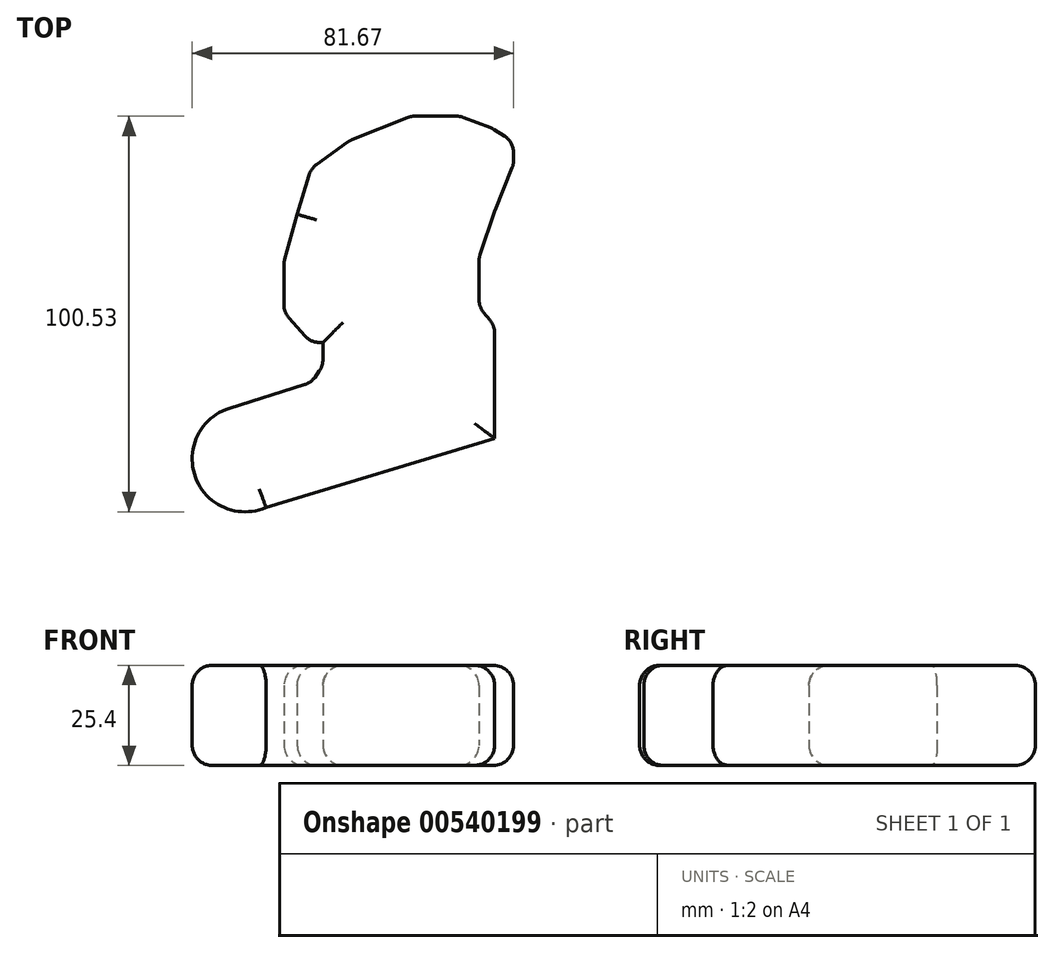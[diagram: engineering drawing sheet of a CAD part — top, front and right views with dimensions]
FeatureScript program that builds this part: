
annotation { "Feature Type Name" : "Feature", "Feature Type Description" : "" }
export const myFeature = defineFeature(function(context is Context, id is Id, definition is map)
    precondition{}
    {
        {
            var Q0;
            Q0=qCreatedBy(makeId("Top.planeOp"),FACE);
            var sketch = newSketch(context, id + "F0", { "sketchPlane" : qUnion([Q0])});
            skLineSegment(sketch, "E0", {"start": v(-11.4, -55.6) * mm, "end": v(46.68, -38.04) * mm});
            skLineSegment(sketch, "E1", {"start": v(46.68, -38.04) * mm, "end": v(46.68, -9.43) * mm});
            skLineSegment(sketch, "E2", {"start": v(46.68, -9.43) * mm, "end": v(42.72, -4.61) * mm});
            skLineSegment(sketch, "E3", {"start": v(42.72, -4.61) * mm, "end": v(42.72, 7.85) * mm});
            skLineSegment(sketch, "E4", {"start": v(42.72, 7.85) * mm, "end": v(46.68, 19.75) * mm});
            skLineSegment(sketch, "E5", {"start": v(46.68, 19.75) * mm, "end": v(51.5, 31.65) * mm});
            skLineSegment(sketch, "E6", {"start": v(51.5, 31.65) * mm, "end": v(51.5, 37.31) * mm});
            skLineSegment(sketch, "E7", {"start": v(0, -23.88) * mm, "end": v(-20.74, -30.4) * mm});
            skArc(sketch, "E8", {"start": v(-20.74, -30.4) * mm, "mid": v(-29.33, -47.91) * mm, "end": v(-11.4, -55.6) * mm});
            skLineSegment(sketch, "E9", {"start": v(0, -23.88) * mm, "end": v(3.06, -19.63) * mm});
            skLineSegment(sketch, "E10", {"start": v(3.06, -19.63) * mm, "end": v(3.06, -13.68) * mm});
            skLineSegment(sketch, "E11", {"start": v(3.06, -13.68) * mm, "end": v(0, -13.68) * mm});
            skLineSegment(sketch, "E12", {"start": v(0, -13.68) * mm, "end": v(-6.86, -6.03) * mm});
            skLineSegment(sketch, "E13", {"start": v(-6.86, -6.03) * mm, "end": v(-6.86, 6.72) * mm});
            skLineSegment(sketch, "E14", {"start": v(-6.86, 6.72) * mm, "end": v(-3.46, 18.9) * mm});
            skLineSegment(sketch, "E15", {"start": v(-3.46, 18.9) * mm, "end": v(0, 30.51) * mm});
            skLineSegment(sketch, "E16", {"start": v(0, 30.51) * mm, "end": v(9.85, 37.6) * mm});
            skLineSegment(sketch, "E17", {"start": v(9.85, 37.6) * mm, "end": v(25.44, 43.83) * mm});
            skLineSegment(sketch, "E18", {"start": v(25.44, 43.83) * mm, "end": v(37.9, 43.83) * mm});
            skLineSegment(sketch, "E19", {"start": v(37.9, 43.83) * mm, "end": v(46.11, 40.71) * mm});
            skLineSegment(sketch, "E20", {"start": v(46.11, 40.71) * mm, "end": v(51.5, 37.31) * mm});
            skSolve(sketch);
        }
        {
            var Q0;
            Q0=makeQuery(id+"F0.imprint","IMPRINT",FACE,{"disambiguationData":[TD([[makeQuery(id+"F0.imprint","IMPRINT",EDGE,{"derivedFrom":sQuery(id+"F0.wireOp",EDGE,"E0")}),1.0]])]});
            extrude(context, id + "F1", {"entities" : qUnion([Q0]), "depth" : 25.4 * mm, "offsetDistance" : 25.4 * mm});
        }
        {
            var Q0;
            Q0=makeQuery(id+"F1.opExtrude","SWEPT_EDGE",EDGE,{"disambiguationData":[OSD([sQuery(id+"F0.wireOp",EDGE,"E16"),sQuery(id+"F0.wireOp",EDGE,"E17")])]});
            var Q1;
            Q1=makeQuery(id+"F1.opExtrude","SWEPT_EDGE",EDGE,{"disambiguationData":[OSD([sQuery(id+"F0.wireOp",EDGE,"E17"),sQuery(id+"F0.wireOp",EDGE,"E18")])]});
            var Q2;
            Q2=makeQuery(id+"F1.opExtrude","SWEPT_EDGE",EDGE,{"disambiguationData":[OSD([sQuery(id+"F0.wireOp",EDGE,"E15"),sQuery(id+"F0.wireOp",EDGE,"E16")])]});
            var Q3;
            Q3=makeQuery(id+"F1.opExtrude","SWEPT_EDGE",EDGE,{"disambiguationData":[OSD([sQuery(id+"F0.wireOp",EDGE,"E13"),sQuery(id+"F0.wireOp",EDGE,"E14")])]});
            var Q4;
            Q4=makeQuery(id+"F1.opExtrude","SWEPT_EDGE",EDGE,{"disambiguationData":[OSD([sQuery(id+"F0.wireOp",EDGE,"E12"),sQuery(id+"F0.wireOp",EDGE,"E13")])]});
            var Q5;
            Q5=makeQuery(id+"F1.opExtrude","SWEPT_EDGE",EDGE,{"disambiguationData":[OSD([sQuery(id+"F0.wireOp",EDGE,"E11"),sQuery(id+"F0.wireOp",EDGE,"E12")])]});
            var Q6;
            Q6=makeQuery(id+"F1.opExtrude","SWEPT_EDGE",EDGE,{"disambiguationData":[OSD([sQuery(id+"F0.wireOp",EDGE,"E7"),sQuery(id+"F0.wireOp",EDGE,"E9")])]});
            var Q7;
            Q7=makeQuery(id+"F1.opExtrude","SWEPT_EDGE",EDGE,{"disambiguationData":[OSD([sQuery(id+"F0.wireOp",EDGE,"E2"),sQuery(id+"F0.wireOp",EDGE,"E3")])]});
            var Q8;
            Q8=makeQuery(id+"F1.opExtrude","SWEPT_EDGE",EDGE,{"disambiguationData":[OSD([sQuery(id+"F0.wireOp",EDGE,"E3"),sQuery(id+"F0.wireOp",EDGE,"E4")])]});
            var Q9;
            Q9=makeQuery(id+"F1.opExtrude","SWEPT_EDGE",EDGE,{"disambiguationData":[OSD([sQuery(id+"F0.wireOp",EDGE,"E4"),sQuery(id+"F0.wireOp",EDGE,"E5")])]});
            var Q10;
            Q10=makeQuery(id+"F1.opExtrude","SWEPT_EDGE",EDGE,{"disambiguationData":[OSD([sQuery(id+"F0.wireOp",EDGE,"E5"),sQuery(id+"F0.wireOp",EDGE,"E6")])]});
            var Q11;
            Q11=makeQuery(id+"F1.opExtrude","SWEPT_EDGE",EDGE,{"disambiguationData":[OSD([sQuery(id+"F0.wireOp",EDGE,"E19"),sQuery(id+"F0.wireOp",EDGE,"E20")])]});
            var Q12;
            Q12=makeQuery(id+"F1.opExtrude","SWEPT_EDGE",EDGE,{"disambiguationData":[OSD([sQuery(id+"F0.wireOp",EDGE,"E18"),sQuery(id+"F0.wireOp",EDGE,"E19")])]});
            var Q13;
            Q13=makeQuery(id+"F1.opExtrude","SWEPT_EDGE",EDGE,{"disambiguationData":[OSD([sQuery(id+"F0.wireOp",EDGE,"E1"),sQuery(id+"F0.wireOp",EDGE,"E2")])]});
            var Q14;
            Q14=makeQuery(id+"F1.opExtrude","SWEPT_EDGE",EDGE,{"disambiguationData":[OSD([sQuery(id+"F0.wireOp",EDGE,"E9"),sQuery(id+"F0.wireOp",EDGE,"E10")])]});
            var Q15;
            Q15=makeQuery(id+"F1.opExtrude","SWEPT_EDGE",EDGE,{"disambiguationData":[OSD([sQuery(id+"F0.wireOp",EDGE,"E6"),sQuery(id+"F0.wireOp",EDGE,"E20")])]});
            fillet(context, id + "F2", {"entities" : qUnion([Q0, Q1, Q2, Q3, Q4, Q5, Q6, Q7, Q8, Q9, Q10, Q11, Q12, Q13, Q14, Q15]), "radius" : 5.08 * mm, "tangentPropagation" : true, "allowEdgeOverflow" : false});
        }
        {
            var Q0;
            Q0=makeQuery(id+"F1.opExtrude","CAP_FACE",FACE,{"disambiguationData":[OSD([sQuery(id+"F0.wireOp",EDGE,"E0"),sQuery(id+"F0.wireOp",EDGE,"E1"),sQuery(id+"F0.wireOp",EDGE,"E2"),sQuery(id+"F0.wireOp",EDGE,"E3"),sQuery(id+"F0.wireOp",EDGE,"E4"),sQuery(id+"F0.wireOp",EDGE,"E5"),sQuery(id+"F0.wireOp",EDGE,"E6"),sQuery(id+"F0.wireOp",EDGE,"E7"),sQuery(id+"F0.wireOp",EDGE,"E8"),sQuery(id+"F0.wireOp",EDGE,"E9"),sQuery(id+"F0.wireOp",EDGE,"E10"),sQuery(id+"F0.wireOp",EDGE,"E11"),sQuery(id+"F0.wireOp",EDGE,"E12"),sQuery(id+"F0.wireOp",EDGE,"E13"),sQuery(id+"F0.wireOp",EDGE,"E14"),sQuery(id+"F0.wireOp",EDGE,"E15"),sQuery(id+"F0.wireOp",EDGE,"E16"),sQuery(id+"F0.wireOp",EDGE,"E17"),sQuery(id+"F0.wireOp",EDGE,"E18"),sQuery(id+"F0.wireOp",EDGE,"E19"),sQuery(id+"F0.wireOp",EDGE,"E20")])],"isStart":true});
            var Q1;
            Q1=makeQuery(id+"F1.opExtrude","CAP_FACE",FACE,{"disambiguationData":[OSD([sQuery(id+"F0.wireOp",EDGE,"E0"),sQuery(id+"F0.wireOp",EDGE,"E1"),sQuery(id+"F0.wireOp",EDGE,"E2"),sQuery(id+"F0.wireOp",EDGE,"E3"),sQuery(id+"F0.wireOp",EDGE,"E4"),sQuery(id+"F0.wireOp",EDGE,"E5"),sQuery(id+"F0.wireOp",EDGE,"E6"),sQuery(id+"F0.wireOp",EDGE,"E7"),sQuery(id+"F0.wireOp",EDGE,"E8"),sQuery(id+"F0.wireOp",EDGE,"E9"),sQuery(id+"F0.wireOp",EDGE,"E10"),sQuery(id+"F0.wireOp",EDGE,"E11"),sQuery(id+"F0.wireOp",EDGE,"E12"),sQuery(id+"F0.wireOp",EDGE,"E13"),sQuery(id+"F0.wireOp",EDGE,"E14"),sQuery(id+"F0.wireOp",EDGE,"E15"),sQuery(id+"F0.wireOp",EDGE,"E16"),sQuery(id+"F0.wireOp",EDGE,"E17"),sQuery(id+"F0.wireOp",EDGE,"E18"),sQuery(id+"F0.wireOp",EDGE,"E19"),sQuery(id+"F0.wireOp",EDGE,"E20")])],"isStart":false});
            fillet(context, id + "F3", {"entities" : qUnion([Q0, Q1]), "radius" : 5.08 * mm, "tangentPropagation" : true, "allowEdgeOverflow" : false});
        }
    });
